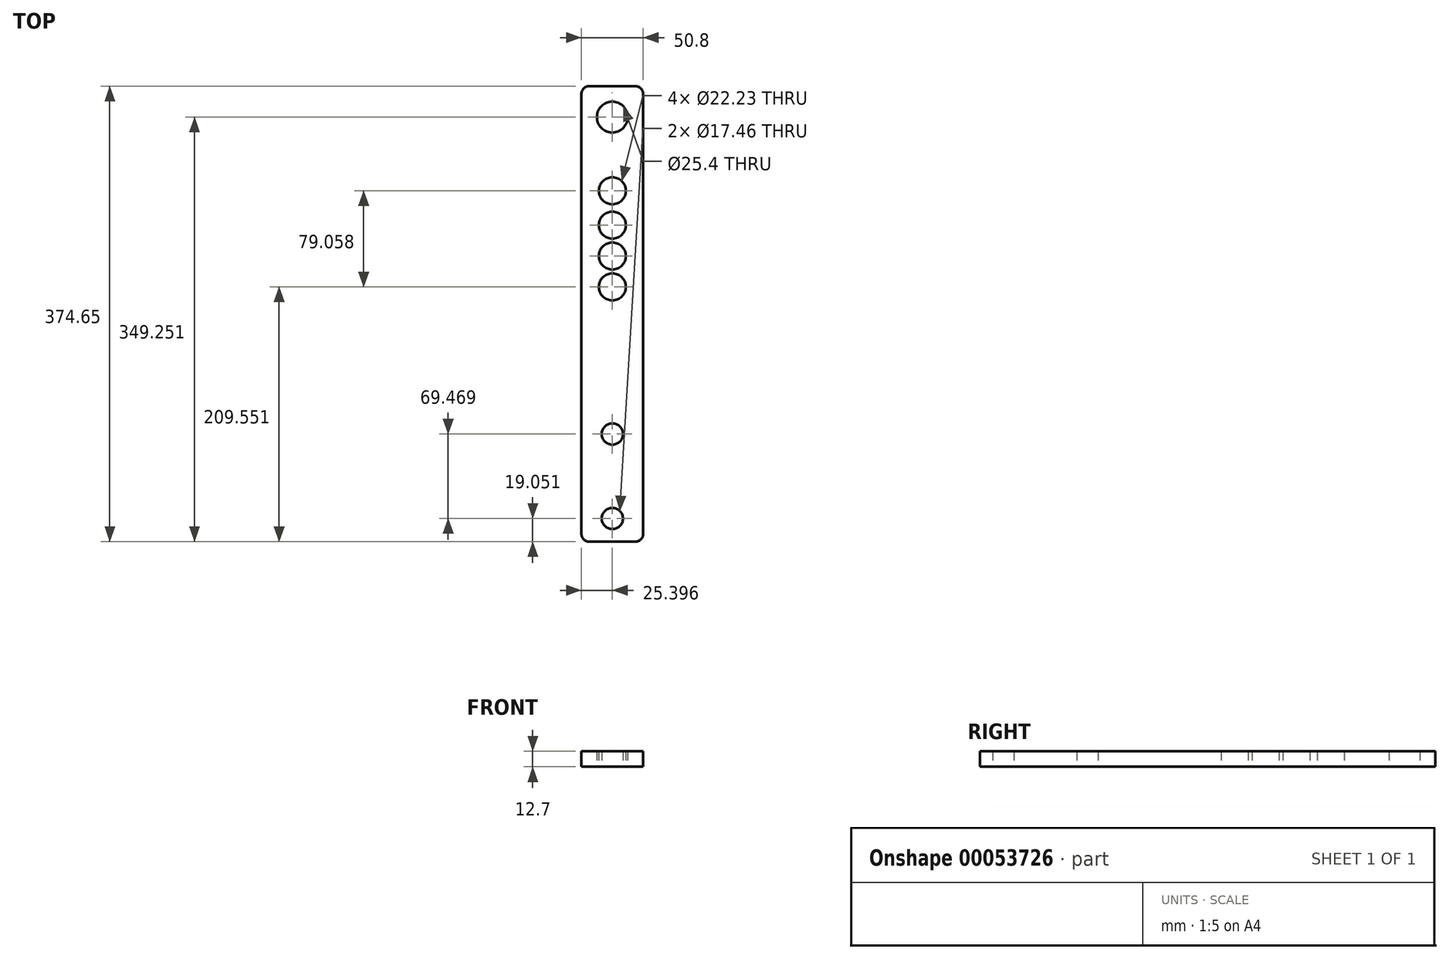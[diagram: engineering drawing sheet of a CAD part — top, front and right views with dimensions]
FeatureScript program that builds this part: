
annotation { "Feature Type Name" : "Feature", "Feature Type Description" : "" }
export const myFeature = defineFeature(function(context is Context, id is Id, definition is map)
    precondition{}
    {
        {
            var Q0;
            Q0=qCreatedBy(makeId("Top.planeOp"),FACE);
            var sketch = newSketch(context, id + "F0", { "sketchPlane" : qUnion([Q0])});
            skLineSegment(sketch, "E0.bottom", {"start": v(-35.21, 286.13) * mm, "end": v(2.89, 286.13) * mm});
            skLineSegment(sketch, "E0.top", {"start": v(-35.21, -88.52) * mm, "end": v(2.89, -88.52) * mm});
            skLineSegment(sketch, "E0.left", {"start": v(-41.56, 279.78) * mm, "end": v(-41.56, -82.17) * mm});
            skLineSegment(sketch, "E0.right", {"start": v(9.24, 279.78) * mm, "end": v(9.24, -82.17) * mm});
            skCircle(sketch, "E1", {"center": v(-16.16, 260.73) * mm, "radius": 12.7 * mm});
            skPoint(sketch, "E1.centerSnap0", {"position": v(-16.16, 286.13) * mm});
            skCircle(sketch, "E2", {"center": v(-16.16, 200.09) * mm, "radius": 11.11 * mm});
            skCircle(sketch, "E3", {"center": v(-16.16, 171.83) * mm, "radius": 11.11 * mm});
            skCircle(sketch, "E4", {"center": v(-16.16, 146.43) * mm, "radius": 11.11 * mm});
            skCircle(sketch, "E5", {"center": v(-16.16, 121.03) * mm, "radius": 11.12 * mm});
            skCircle(sketch, "E6", {"center": v(-16.16, 0) * mm, "radius": 8.73 * mm});
            skCircle(sketch, "E7", {"center": v(-16.16, -69.47) * mm, "radius": 8.73 * mm});
            skPoint(sketch, "E8.visualSharp", {"position": v(-41.56, 286.13) * mm});
            skArc(sketch, "E8.filletArc", {"start": v(-35.21, 286.13) * mm, "mid": v(-39.7, 284.27) * mm, "end": v(-41.56, 279.78) * mm});
            skPoint(sketch, "E9.visualSharp", {"position": v(9.24, 286.13) * mm});
            skArc(sketch, "E9.filletArc", {"start": v(9.24, 279.78) * mm, "mid": v(7.38, 284.27) * mm, "end": v(2.89, 286.13) * mm});
            skPoint(sketch, "E10.visualSharp", {"position": v(9.24, -88.52) * mm});
            skArc(sketch, "E10.filletArc", {"start": v(2.89, -88.52) * mm, "mid": v(7.38, -86.66) * mm, "end": v(9.24, -82.17) * mm});
            skPoint(sketch, "E11.visualSharp", {"position": v(-41.56, -88.52) * mm});
            skArc(sketch, "E11.filletArc", {"start": v(-41.56, -82.17) * mm, "mid": v(-39.7, -86.66) * mm, "end": v(-35.21, -88.52) * mm});
            skSolve(sketch);
        }
        {
            var Q0;
            Q0=makeQuery(id+"F0.imprint","IMPRINT",FACE,{"disambiguationData":[TD([[makeQuery(id+"F0.imprint","IMPRINT",EDGE,{"derivedFrom":sQuery(id+"F0.wireOp",EDGE,"E0.bottom")}),-1.0]])]});
            extrude(context, id + "F1", {"entities" : qUnion([Q0]), "depth" : 12.7 * mm});
        }
    });
